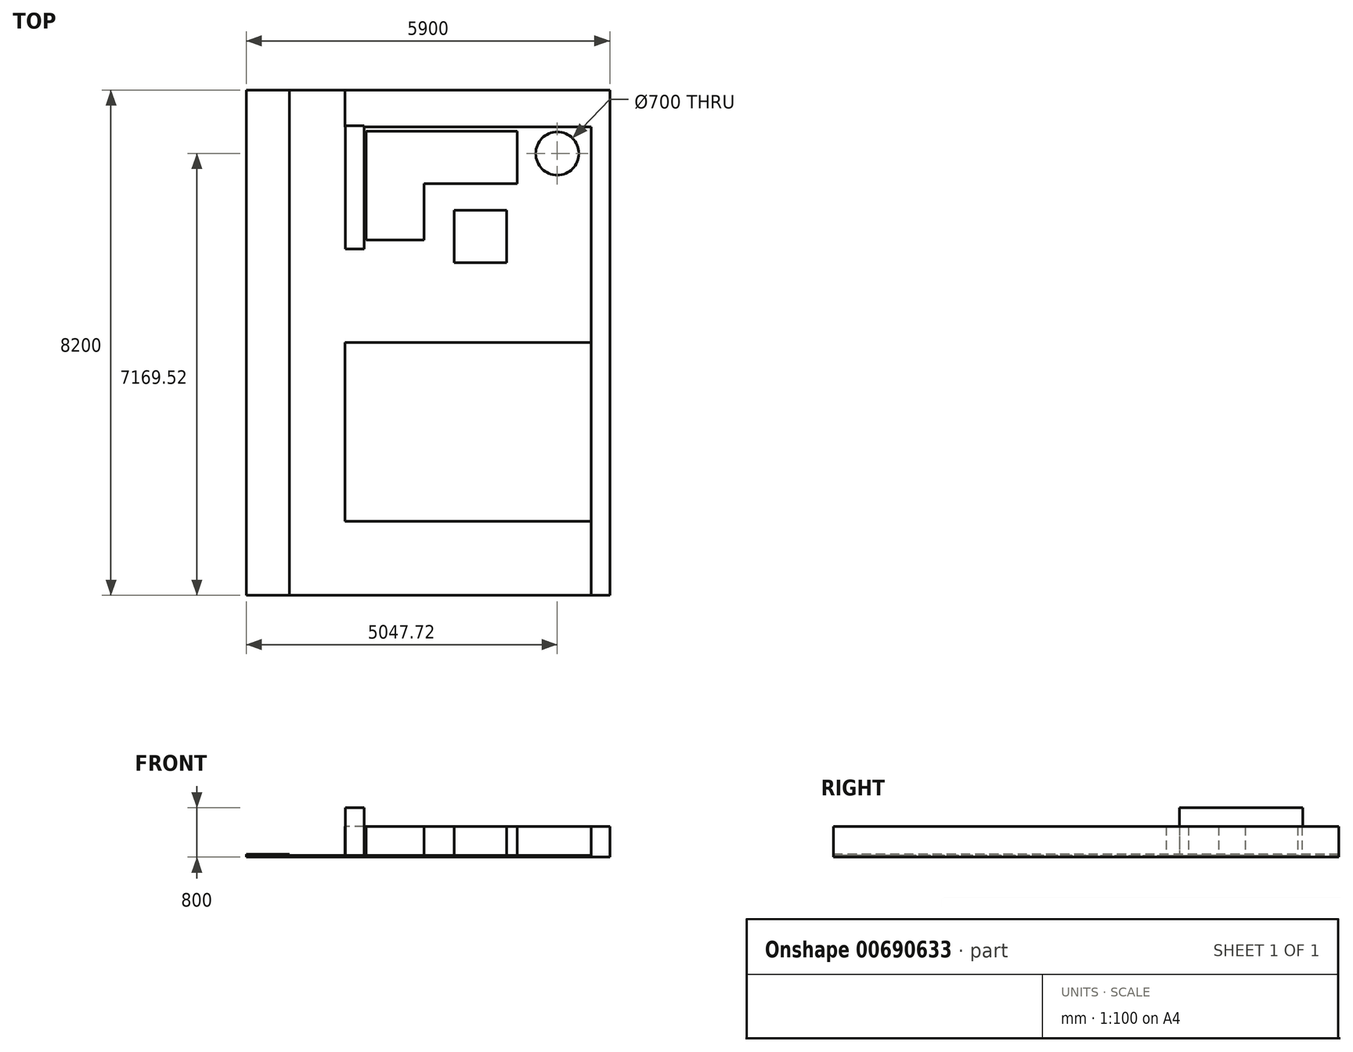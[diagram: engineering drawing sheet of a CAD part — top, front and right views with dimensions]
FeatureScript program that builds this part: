
annotation { "Feature Type Name" : "Feature", "Feature Type Description" : "" }
export const myFeature = defineFeature(function(context is Context, id is Id, definition is map)
    precondition{}
    {
        {
            var Q0;
            Q0=qCreatedBy(makeId("Top.planeOp"),FACE);
            var sketch = newSketch(context, id + "F0", { "sketchPlane" : qUnion([Q0])});
            skLineSegment(sketch, "E0.bottom", {"start": v(0, 0) * mm, "end": v(5900, 0) * mm});
            skLineSegment(sketch, "E0.top", {"start": v(0, -8200) * mm, "end": v(5900, -8200) * mm});
            skLineSegment(sketch, "E0.left", {"start": v(0, 0) * mm, "end": v(0, -8200) * mm});
            skLineSegment(sketch, "E0.right", {"start": v(5900, 0) * mm, "end": v(5900, -8200) * mm});
            skLineSegment(sketch, "E1", {"start": v(700, 0) * mm, "end": v(700, -8200) * mm});
            skLineSegment(sketch, "E2", {"start": v(1600, 0) * mm, "end": v(1600, -600) * mm});
            skLineSegment(sketch, "E3", {"start": v(1600, -7000) * mm, "end": v(2500, -7000) * mm});
            skLineSegment(sketch, "E4", {"start": v(2500, -7000) * mm, "end": v(2500, -7000) * mm});
            skLineSegment(sketch, "E5", {"start": v(2500, -7000) * mm, "end": v(5600, -7000) * mm});
            skLineSegment(sketch, "E6", {"start": v(5600, -7000) * mm, "end": v(5600, -8200) * mm});
            skLineSegment(sketch, "E7", {"start": v(5600, -7000) * mm, "end": v(5600, 0) * mm});
            skLineSegment(sketch, "E8", {"start": v(1600, -600) * mm, "end": v(5600, -600) * mm});
            skLineSegment(sketch, "E9", {"start": v(5600, -600) * mm, "end": v(5600, -4100) * mm});
            skLineSegment(sketch, "E10", {"start": v(5600, -4100) * mm, "end": v(1600, -4100) * mm});
            skLineSegment(sketch, "E11", {"start": v(5600, -600) * mm, "end": v(5600, -600) * mm});
            skCircle(sketch, "E12", {"center": v(5047.72, -1030.48) * mm, "radius": 350 * mm});
            skLineSegment(sketch, "E13", {"start": v(4500, -600) * mm, "end": v(4500, -1600) * mm, "construction": true});
            skLineSegment(sketch, "E14", {"start": v(4500, -1600) * mm, "end": v(5600, -1600) * mm, "construction": true});
            skLineSegment(sketch, "E15.trimOffspring", {"start": v(1600, -4100) * mm, "end": v(1600, -7000) * mm});
            skSolve(sketch);
        }
        {
            var Q0;
            {var subQ0=sQuery(id+"F0.wireOp",EDGE,"E2");Q0=makeQuery(id+"F0.imprint","IMPRINT",FACE,{"disambiguationData":[TD([[makeQuery(id+"F0.imprint","IMPRINT",EDGE,{"derivedFrom":subQ0}),1.0]])]});}
            var Q1;
            {var subQ0=sQuery(id+"F0.wireOp",EDGE,"E0.right");Q1=makeQuery(id+"F0.imprint","IMPRINT",FACE,{"disambiguationData":[TD([[makeQuery(id+"F0.imprint","IMPRINT",EDGE,{"derivedFrom":subQ0}),-1.0]])]});}
            extrude(context, id + "F1", {"entities" : qUnion([Q0, Q1]), "depth" : 500 * mm, "offsetDistance" : 25 * mm});
        }
        {
            var Q0;
            {var subQ6=sQuery(id+"F0.wireOp",EDGE,"E1");Q0=makeQuery(id+"F0.imprint","IMPRINT",FACE,{"disambiguationData":[TD([[makeQuery(id+"F0.imprint","IMPRINT",EDGE,{"derivedFrom":subQ6}),1.0]])]});}
            extrude(context, id + "F2", {"entities" : qUnion([Q0]), "depth" : 25 * mm, "offsetDistance" : 25 * mm});
        }
        {
            var Q0;
            {var subQ0=sQuery(id+"F0.wireOp",EDGE,"E0.left");Q0=makeQuery(id+"F0.imprint","IMPRINT",FACE,{"disambiguationData":[TD([[makeQuery(id+"F0.imprint","IMPRINT",EDGE,{"derivedFrom":subQ0}),1.0]])]});}
            extrude(context, id + "F3", {"entities" : qUnion([Q0]), "depth" : 45 * mm, "offsetDistance" : 25 * mm});
        }
        {
            var Q0;
            Q0=makeQuery(id+"F0.imprint","IMPRINT",FACE,{"disambiguationData":[TD([[makeQuery(id+"F0.imprint","IMPRINT",EDGE,{"derivedFrom":sQuery(id+"F0.wireOp",EDGE,"E3")}),1.0]])]});
            extrude(context, id + "F4", {"entities" : qUnion([Q0]), "depth" : 30 * mm, "offsetDistance" : 25 * mm});
        }
        {
            var Q0;
            Q0=qCreatedBy(makeId("Top.planeOp"),FACE);
            var sketch = newSketch(context, id + "F5", { "sketchPlane" : qUnion([Q0])});
            skLineSegment(sketch, "E16.bottom", {"start": v(1947.92, -667.34) * mm, "end": v(4397.92, -667.34) * mm});
            skLineSegment(sketch, "E16.top", {"start": v(1947.92, -1517.34) * mm, "end": v(4397.92, -1517.34) * mm});
            skLineSegment(sketch, "E16.left", {"start": v(1947.92, -667.34) * mm, "end": v(1947.92, -1517.34) * mm});
            skLineSegment(sketch, "E16.right", {"start": v(4397.92, -667.34) * mm, "end": v(4397.92, -1517.34) * mm});
            skLineSegment(sketch, "E17", {"start": v(1947.92, -1517.34) * mm, "end": v(1947.92, -2436.09) * mm});
            skLineSegment(sketch, "E18", {"start": v(1947.92, -2436.09) * mm, "end": v(2887.03, -2436.09) * mm});
            skLineSegment(sketch, "E19", {"start": v(2887.03, -2436.09) * mm, "end": v(2887.03, -1517.34) * mm});
            skLineSegment(sketch, "E20.bottom", {"start": v(3376, -1949.94) * mm, "end": v(4226, -1949.94) * mm});
            skLineSegment(sketch, "E20.top", {"start": v(3376, -2799.94) * mm, "end": v(4226, -2799.94) * mm});
            skLineSegment(sketch, "E20.left", {"start": v(3376, -1949.94) * mm, "end": v(3376, -2799.94) * mm});
            skLineSegment(sketch, "E20.right", {"start": v(4226, -1949.94) * mm, "end": v(4226, -2799.94) * mm});
            skSolve(sketch);
        }
        {
            var Q0;
            Q0 = qSketchRegion(id + "F5", true);
            extrude(context, id + "F6", {"entities" : qUnion([Q0]), "operationType" : NewBodyOperationType.ADD, "depth" : 500 * mm, "offsetDistance" : 25 * mm});
        }
        {
            var Q0;
            Q0=qCreatedBy(makeId("Top.planeOp"),FACE);
            var sketch = newSketch(context, id + "F7", { "sketchPlane" : qUnion([Q0])});
            skLineSegment(sketch, "E21.bottom", {"start": v(1611.91, -581.63) * mm, "end": v(1911.91, -581.63) * mm});
            skLineSegment(sketch, "E21.top", {"start": v(1611.91, -2581.63) * mm, "end": v(1911.91, -2581.63) * mm});
            skLineSegment(sketch, "E21.left", {"start": v(1611.91, -581.63) * mm, "end": v(1611.91, -2581.63) * mm});
            skLineSegment(sketch, "E21.right", {"start": v(1911.91, -581.63) * mm, "end": v(1911.91, -2581.63) * mm});
            skSolve(sketch);
        }
        {
            var Q0;
            Q0 = qSketchRegion(id + "F7", true);
            extrude(context, id + "F8", {"entities" : qUnion([Q0]), "operationType" : NewBodyOperationType.ADD, "depth" : 800 * mm, "offsetDistance" : 25 * mm});
        }
    });
